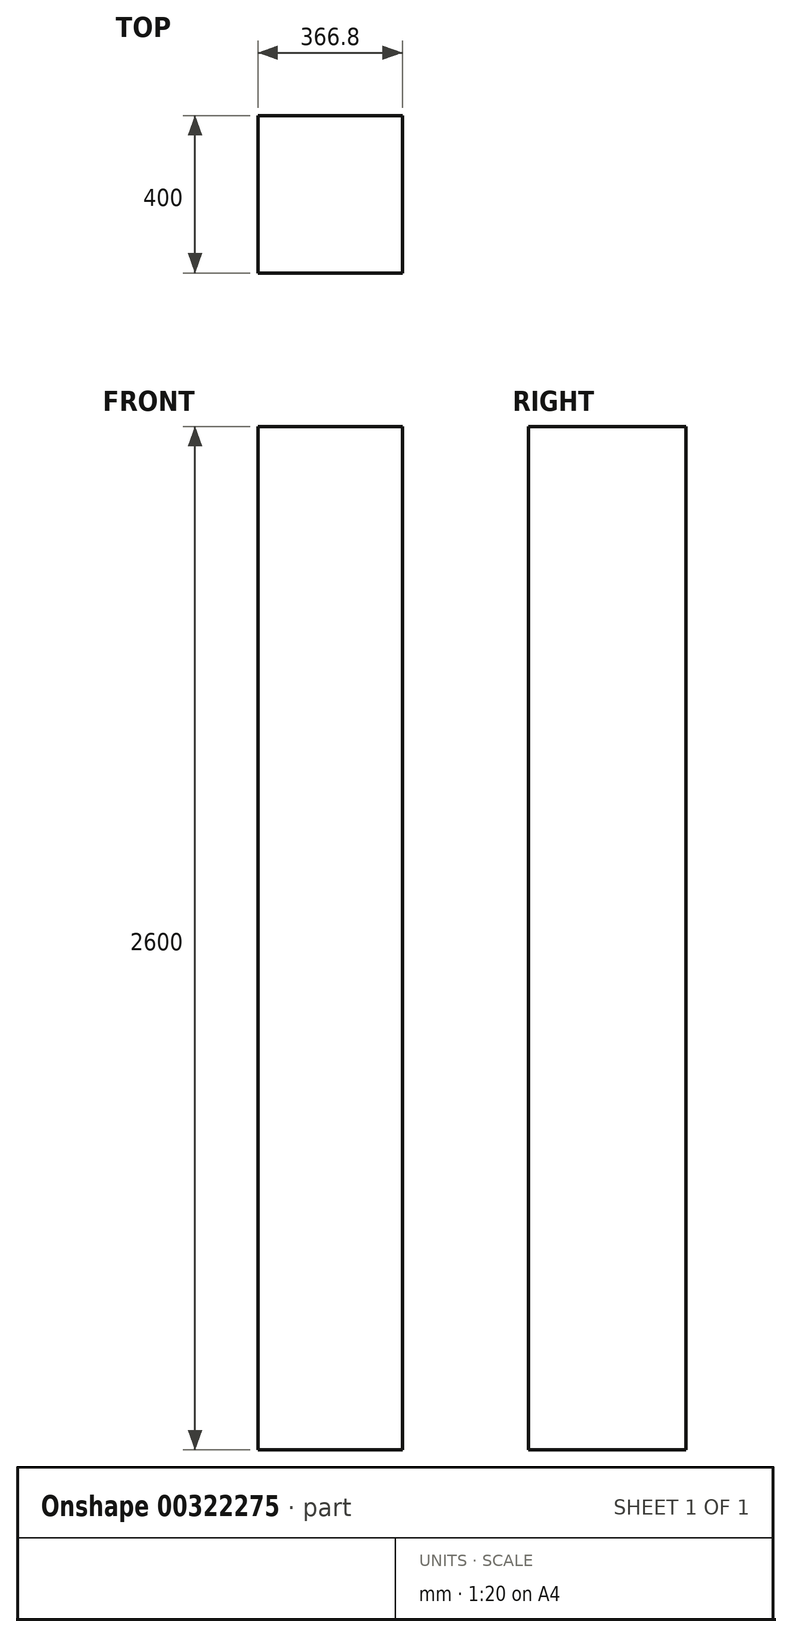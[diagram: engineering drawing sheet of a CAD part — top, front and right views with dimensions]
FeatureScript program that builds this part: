
annotation { "Feature Type Name" : "Feature", "Feature Type Description" : "" }
export const myFeature = defineFeature(function(context is Context, id is Id, definition is map)
    precondition{}
    {
        {
            var Q0;
            Q0=qCreatedBy(makeId("Top.planeOp"),FACE);
            var sketch = newSketch(context, id + "F0", { "sketchPlane" : qUnion([Q0])});
            skLineSegment(sketch, "E0", {"start": v(0, 0) * mm, "end": v(3633.2, 0) * mm});
            skLineSegment(sketch, "E1", {"start": v(4000, 0) * mm, "end": v(4000, -400) * mm});
            skLineSegment(sketch, "E2", {"start": v(4000, -400) * mm, "end": v(8000, -400) * mm});
            skLineSegment(sketch, "E3", {"start": v(8000, -400) * mm, "end": v(8000, -3313.7) * mm});
            skLineSegment(sketch, "E4", {"start": v(8000, -3313.7) * mm, "end": v(0, -3313.7) * mm});
            skLineSegment(sketch, "E5", {"start": v(0, -3313.7) * mm, "end": v(0, 0) * mm});
            skLineSegment(sketch, "E6.bottom", {"start": v(4000, 0) * mm, "end": v(3633.2, 0) * mm});
            skLineSegment(sketch, "E7", {"start": v(3633.2, 0) * mm, "end": v(3633.2, -400) * mm});
            skLineSegment(sketch, "E8", {"start": v(3633.2, -400) * mm, "end": v(4000, -400) * mm});
            skLineSegment(sketch, "E9.0", {"start": v(0, -200) * mm, "end": v(3633.2, -200) * mm});
            skSolve(sketch);
        }
        {
            var Q0;
            Q0=makeQuery(id+"F0.imprint","IMPRINT",FACE,{"disambiguationData":[TD([[makeQuery(id+"F0.imprint","IMPRINT",EDGE,{"derivedFrom":sQuery(id+"F0.wireOp",EDGE,"E2")}),-1.0]])]});
            var sketch = newSketch(context, id + "F1", { "sketchPlane" : qUnion([Q0])});
            skSolve(sketch);
        }
        {
            var Q0;
            {var subQ3=sQuery(id+"F0.wireOp",EDGE,"E6.bottom");Q0=makeQuery(id+"F0.imprint","IMPRINT",FACE,{"disambiguationData":[TD([[makeQuery(id+"F0.imprint","IMPRINT",EDGE,{"derivedFrom":subQ3}),1.0]])]});}
            extrude(context, id + "F2", {"entities" : qUnion([Q0]), "depth" : 2600 * mm});
        }
    });
